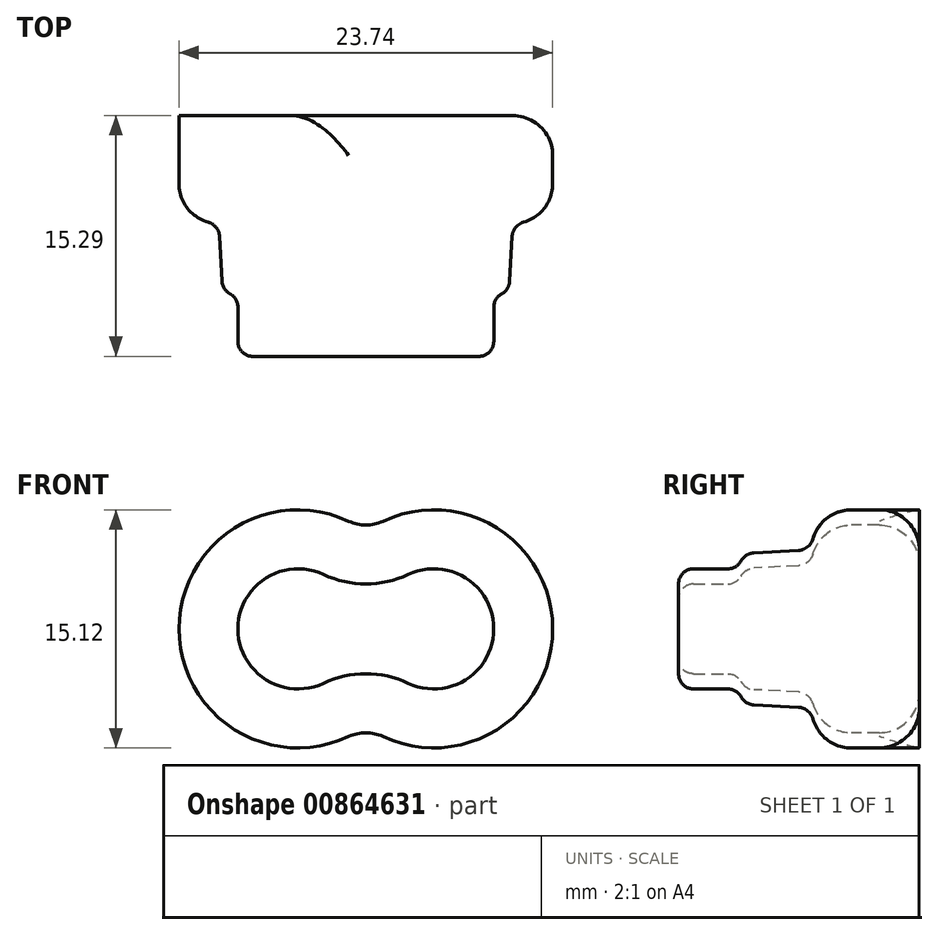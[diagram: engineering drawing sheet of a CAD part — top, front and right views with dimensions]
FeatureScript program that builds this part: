
annotation { "Feature Type Name" : "Feature", "Feature Type Description" : "" }
export const myFeature = defineFeature(function(context is Context, id is Id, definition is map)
    precondition{}
    {
        {
            var Q0;
            Q0=qCreatedBy(makeId("Front.planeOp"),FACE);
            var sketch = newSketch(context, id + "F0", { "sketchPlane" : qUnion([Q0])});
            skArc(sketch, "E0", {"start": v(-49.58, 31.14) * mm, "mid": v(-61.45, 24.93) * mm, "end": v(-49.58, 18.72) * mm});
            skLineSegment(sketch, "E1", {"start": v(-49.58, 35.7) * mm, "end": v(-49.58, 14.16) * mm, "construction": true});
            skArc(sketch, "E2.MirrorCS", {"start": v(-49.58, 31.14) * mm, "mid": v(-37.7, 24.93) * mm, "end": v(-49.58, 18.72) * mm});
            skSolve(sketch);
        }
        {
            var Q0;
            Q0=makeQuery(id+"F0.imprint","IMPRINT",FACE,{"disambiguationData":[TD([[makeQuery(id+"F0.imprint","IMPRINT",EDGE,{"derivedFrom":sQuery(id+"F0.wireOp",EDGE,"E0")}),1.0]])]});
            extrude(context, id + "F1", {"entities" : qUnion([Q0]), "depth" : 6.86 * mm, "offsetDistance" : 25.4 * mm});
        }
        {
            var Q0;
            Q0=makeQuery(id+"F1.opExtrude","CAP_EDGE",EDGE,{"disambiguationData":[OSD([sQuery(id+"F0.wireOp",EDGE,"E0")])],"isStart":false});
            var Q1;
            Q1=makeQuery(id+"F1.opExtrude","CAP_EDGE",EDGE,{"disambiguationData":[OSD([sQuery(id+"F0.wireOp",EDGE,"E2.MirrorCS")])],"isStart":false});
            var Q2;
            Q2=makeQuery(id+"F1.opExtrude","SWEPT_FACE",FACE,{"disambiguationData":[OSD([sQuery(id+"F0.wireOp",EDGE,"E2.MirrorCS")])]});
            var Q3;
            Q3=makeQuery(id+"F1.opExtrude","CAP_FACE",FACE,{"disambiguationData":[OSD([sQuery(id+"F0.wireOp",EDGE,"E0"),sQuery(id+"F0.wireOp",EDGE,"E2.MirrorCS")])],"isStart":false});
            fillet(context, id + "F2", {"entities" : qUnion([Q0, Q1, Q2, Q3]), "radius" : 2.54 * mm, "tangentPropagation" : true, "allowEdgeOverflow" : false});
        }
        {
            var Q0;
            Q0=makeQuery(id+"F1.opExtrude","CAP_FACE",FACE,{"disambiguationData":[OSD([sQuery(id+"F0.wireOp",EDGE,"E0"),sQuery(id+"F0.wireOp",EDGE,"E2.MirrorCS")])],"isStart":false});
            extrude(context, id + "F3", {"entities" : qUnion([Q0]), "operationType" : NewBodyOperationType.ADD, "depth" : 4.6 * mm, "offsetDistance" : 25.4 * mm, "hasDraft" : true, "draftAngle" : 3 * degree, "draftPullDirection" : true});
        }
        {
            var Q0;
            {var subQ0=sQuery(id+"F0.wireOp",EDGE,"E2.MirrorCS");var subQ1=sQuery(id+"F0.wireOp",EDGE,"E0");Q0=makeQuery(id+"F3.opExtrude","SWEPT_FACE",FACE,{"disambiguationData":[OSD([subQ1,subQ0]),TDD([makeQuery(id+"F2.opFillet","BLEND_EDGE",EDGE,{"blendedFrom":[makeQuery(id+"F1.opExtrude","CAP_EDGE",EDGE,{"disambiguationData":[OSD([subQ1])],"isStart":false}),makeQuery(id+"F1.opExtrude","CAP_FACE",FACE,{"disambiguationData":[OSD([subQ1,subQ0])],"isStart":false})],"blendedInto":[makeQuery(id+"F1.opExtrude","CAP_FACE",FACE,{"disambiguationData":[OSD([subQ1,subQ0])],"isStart":false})]})])]});}
            var Q1;
            {var subQ0=sQuery(id+"F0.wireOp",EDGE,"E2.MirrorCS");var subQ1=sQuery(id+"F0.wireOp",EDGE,"E0");Q1=makeQuery(id+"F3.opExtrude","SWEPT_FACE",FACE,{"disambiguationData":[OSD([subQ1,subQ0]),TDD([makeQuery(id+"F2.opFillet","BLEND_EDGE",EDGE,{"blendedFrom":[makeQuery(id+"F1.opExtrude","CAP_EDGE",EDGE,{"disambiguationData":[OSD([subQ0])],"isStart":false}),makeQuery(id+"F1.opExtrude","CAP_FACE",FACE,{"disambiguationData":[OSD([subQ1,subQ0])],"isStart":false})],"blendedInto":[makeQuery(id+"F1.opExtrude","CAP_FACE",FACE,{"disambiguationData":[OSD([subQ1,subQ0])],"isStart":false})]})])]});}
            fillet(context, id + "F4", {"entities" : qUnion([Q0, Q1]), "radius" : 1.02 * mm, "tangentPropagation" : true, "allowEdgeOverflow" : false});
        }
        {
            var Q0;
            Q0=makeQuery(id+"F3.opExtrude","CAP_FACE",FACE,{"disambiguationData":[OSD([sQuery(id+"F0.wireOp",EDGE,"E0"),sQuery(id+"F0.wireOp",EDGE,"E2.MirrorCS")])],"isStart":false});
            extrude(context, id + "F5", {"entities" : qUnion([Q0]), "operationType" : NewBodyOperationType.ADD, "depth" : 3.84 * mm, "offsetDistance" : 25.4 * mm});
        }
        {
            var Q0;
            {var subQ0=sQuery(id+"F0.wireOp",EDGE,"E2.MirrorCS");var subQ1=sQuery(id+"F0.wireOp",EDGE,"E0");Q0=makeQuery(id+"F5.opExtrude","SWEPT_FACE",FACE,{"disambiguationData":[OSD([subQ1,subQ0]),TDD([makeQuery(id+"F4.opFillet","BLEND_EDGE",EDGE,{"blendedFrom":[makeQuery(id+"F3.opExtrude","CAP_EDGE",EDGE,{"disambiguationData":[OSD([subQ1,subQ0]),TDD([makeQuery(id+"F2.opFillet","BLEND_EDGE",EDGE,{"blendedFrom":[makeQuery(id+"F1.opExtrude","CAP_EDGE",EDGE,{"disambiguationData":[OSD([subQ1])],"isStart":false}),makeQuery(id+"F1.opExtrude","CAP_FACE",FACE,{"disambiguationData":[OSD([subQ1,subQ0])],"isStart":false})],"blendedInto":[makeQuery(id+"F1.opExtrude","CAP_FACE",FACE,{"disambiguationData":[OSD([subQ1,subQ0])],"isStart":false})]})])],"isStart":false}),makeQuery(id+"F3.opExtrude","CAP_FACE",FACE,{"disambiguationData":[OSD([subQ1,subQ0])],"isStart":false})],"blendedInto":[makeQuery(id+"F3.opExtrude","CAP_FACE",FACE,{"disambiguationData":[OSD([subQ1,subQ0])],"isStart":false})]})])]});}
            fillet(context, id + "F6", {"entities" : qUnion([Q0]), "radius" : 0.94 * mm, "tangentPropagation" : true, "allowEdgeOverflow" : false});
        }
    });
